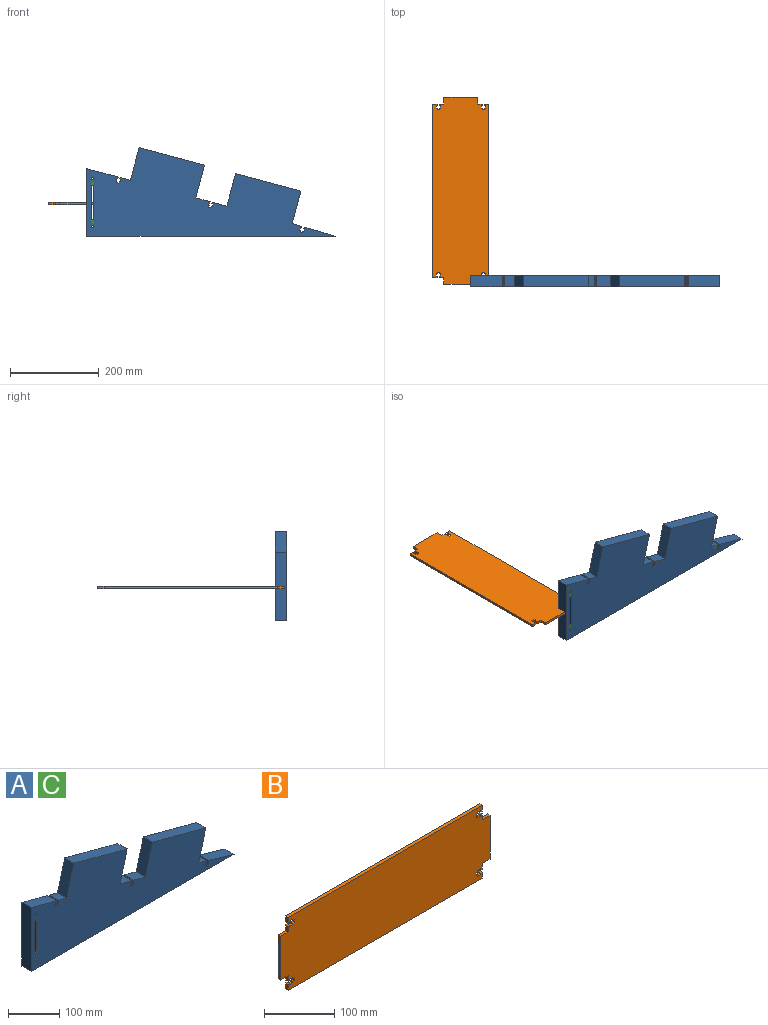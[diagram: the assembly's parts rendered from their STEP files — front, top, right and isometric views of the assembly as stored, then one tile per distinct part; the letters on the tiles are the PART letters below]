
ASSEMBLY  parts=3 mates=2
PART A: 55 faces, bbox 560.1x25.4x199.7 mm
  f0: plane 25.4x3.07mm, normal (-0.97,0,0.26), area 80.8mm2, adj f1,f52,f53,f54
  f1: plane 25.4x2.16mm, normal (-0.26,0,-0.97), area 56.8mm2, adj f0,f2,f53,f54
  f2: plane 25.4x6.11mm, normal (-0.97,0,0.26), area 160.6mm2, adj f1,f3,f53,f54
  f3: plane 25.4x2.16mm, normal (0.26,0,0.97), area 56.8mm2, adj f2,f4,f53,f54
  f4: plane 25.4x3.09mm, normal (-0.97,0,0.26), area 81.1mm2, adj f3,f5,f53,f54
  f5: plane 25.4x4.91mm, normal (0.26,0,0.97), area 129mm2, adj f4,f6,f53,f54
  f6: plane 25.4x3.11mm, normal (0.97,0,-0.26), area 81.7mm2, adj f5,f7,f53,f54
  f7: plane 25.4x2.16mm, normal (0.26,0,0.97), area 56.8mm2, adj f6,f8,f53,f54
  f8: plane 25.4x6.11mm, normal (0.97,0,-0.26), area 160.6mm2, adj f7,f9,f53,f54
  f9: plane 25.4x2.16mm, normal (-0.26,0,-0.97), area 56.8mm2, adj f8,f10,f53,f54
  f10: plane 25.4x3.05mm, normal (0.97,0,-0.26), area 80.3mm2, adj f9,f11,f53,f54
  f11: plane 70.28x25.4mm, normal (0.26,0,0.97), area 1848.2mm2, adj f10,f12,f53,f54
  f12: plane 152.4x25.4mm, normal (-1,0,0), area 3871mm2, adj f11,f13,f53,f54
  f13: plane 560.09x25.4mm, normal (0,0,-1), area 14226.3mm2, adj f12,f14,f53,f54
  f14: plane 70.86x25.4mm, normal (0.28,0,0.96), area 1874.8mm2, adj f13,f15,f53,f54
  f15: plane 25.4x3.06mm, normal (-0.96,0,0.28), area 81mm2, adj f14,f16,f53,f54
  f16: plane 25.4x2.15mm, normal (-0.28,0,-0.96), area 56.8mm2, adj f15,f17,f53,f54
  f17: plane 25.4x6.07mm, normal (-0.96,0,0.28), area 160.6mm2, adj f16,f18,f53,f54
  f18: plane 25.4x2.15mm, normal (0.28,0,0.96), area 56.8mm2, adj f17,f19,f53,f54
  f19: plane 25.4x3.06mm, normal (-0.96,0,0.28), area 81mm2, adj f18,f20,f53,f54
  f20: plane 25.4x4.73mm, normal (0.28,0,0.96), area 125.1mm2, adj f19,f21,f53,f54
  f21: plane 25.4x3.06mm, normal (0.96,0,-0.28), area 81mm2, adj f20,f22,f53,f54
  f22: plane 25.4x2.15mm, normal (0.28,0,0.96), area 56.8mm2, adj f21,f23,f53,f54
  f23: plane 25.4x6.07mm, normal (0.96,0,-0.28), area 160.6mm2, adj f22,f24,f53,f54
  f24: plane 25.4x2.15mm, normal (-0.28,0,-0.96), area 56.8mm2, adj f23,f25,f53,f54
  f25: plane 25.4x3.06mm, normal (0.96,0,-0.28), area 81mm2, adj f24,f26,f53,f54
  f26: plane 25.4x21.97mm, normal (0.28,0,0.96), area 581.3mm2, adj f25,f27,f53,f54
  f27: plane 73.6x25.4mm, normal (0.97,0,-0.26), area 1935.5mm2, adj f26,f28,f53,f54
  f28: plane 147.21x39.44mm, normal (0.26,0,0.97), area 3871mm2, adj f27,f29,f53,f54
  f29: plane 73.6x25.4mm, normal (-0.97,0,0.26), area 1935.5mm2, adj f28,f30,f53,f54
  f30: plane 32.66x25.4mm, normal (0.26,0,0.97), area 859mm2, adj f29,f31,f53,f54
  f31: plane 25.4x3.08mm, normal (-0.97,0,0.26), area 81mm2, adj f30,f32,f53,f54
  f32: plane 25.4x2.16mm, normal (-0.26,0,-0.97), area 56.8mm2, adj f31,f33,f53,f54
  f33: plane 25.4x6.11mm, normal (-0.97,0,0.26), area 160.6mm2, adj f32,f34,f53,f54
  f34: plane 25.4x2.16mm, normal (0.26,0,0.97), area 56.8mm2, adj f33,f35,f53,f54
  f35: plane 25.4x3.08mm, normal (-0.97,0,0.26), area 81mm2, adj f34,f36,f53,f54
  f36: plane 25.4x4.66mm, normal (0.26,0,0.97), area 122.6mm2, adj f35,f37,f53,f54
  f37: plane 25.4x3.08mm, normal (0.97,0,-0.26), area 81mm2, adj f36,f38,f53,f54
  f38: plane 25.4x2.16mm, normal (0.26,0,0.97), area 56.8mm2, adj f37,f39,f53,f54
  f39: plane 25.4x6.11mm, normal (0.97,0,-0.26), area 160.6mm2, adj f38,f40,f53,f54
  f40: plane 25.4x2.16mm, normal (-0.26,0,-0.97), area 56.8mm2, adj f39,f41,f53,f54
  f41: plane 25.4x3.08mm, normal (0.97,0,-0.26), area 81mm2, adj f40,f42,f53,f54
  f42: plane 32.66x25.4mm, normal (0.26,0,0.97), area 858.7mm2, adj f41,f43,f53,f54
  f43: plane 73.6x25.4mm, normal (0.97,0,-0.26), area 1935.5mm2, adj f42,f44,f53,f54
  f44: plane 147.21x39.44mm, normal (0.26,0,0.97), area 3871mm2, adj f43,f45,f53,f54
  f45: plane 73.6x25.4mm, normal (-0.97,0,0.26), area 1935.5mm2, adj f44,f52,f53,f54
  f46: plane 76.2x25.4mm, normal (-1,0,0), area 1935.5mm2, adj f47,f51,f53,f54
  f47: plane 25.4x5.08mm, normal (0,0,1), area 129mm2, adj f46,f48,f53,f54
  f48: plane 76.2x25.4mm, normal (1,0,0), area 1935.5mm2, adj f47,f51,f53,f54
  f49: cylinder r=2.54mm len=25.4mm, axis (0,1,0), area 405.4mm2, adj f53,f54
  f50: cylinder r=2.54mm len=25.4mm, axis (0,1,0), area 405.4mm2, adj f53,f54
  f51: plane 25.4x5.08mm, normal (0,0,-1), area 129mm2, adj f46,f48,f53,f54
  f52: plane 25.4x22.95mm, normal (0.26,0,0.97), area 603.4mm2, adj f0,f45,f53,f54
  f53: plane 560.09x199.71mm, normal (0,-1,0), area 65741.3mm2, adj f0,f1,f2,f3,f4,f5,f6,f7
  f54: plane 560.09x199.71mm, normal (0,1,0), area 65741.3mm2, adj f0,f1,f2,f3,f4,f5,f6,f7
PART B: 62 faces, bbox 421.6x5.1x127 mm
  f0: plane 76.2x5.08mm, normal (-1,0,0), area 387.1mm2, adj f1,f59,f60,f61
  f1: plane 15.24x5.08mm, normal (0,0,-1), area 77.4mm2, adj f0,f2,f60,f61
  f2: plane 10.16x5.08mm, normal (-1,0,0), area 51.6mm2, adj f1,f3,f60,f61
  f3: plane 5.08x3.19mm, normal (0,0,-1), area 16.2mm2, adj f2,f4,f60,f61
  f4: plane 5.08x2.24mm, normal (1,0,0), area 11.4mm2, adj f3,f5,f60,f61
  f5: plane 6.32x5.08mm, normal (0,0,-1), area 32.1mm2, adj f4,f6,f60,f61
  f6: plane 5.08x2.24mm, normal (-1,0,0), area 11.4mm2, adj f5,f7,f60,f61
  f7: plane 5.08x3.19mm, normal (0,0,-1), area 16.2mm2, adj f6,f8,f60,f61
  f8: plane 5.08x5.08mm, normal (-1,0,0), area 25.8mm2, adj f7,f9,f60,f61
  f9: plane 5.08x3.19mm, normal (0,0,1), area 16.2mm2, adj f8,f10,f60,f61
  f10: plane 5.08x2.24mm, normal (-1,0,0), area 11.4mm2, adj f9,f11,f60,f61
  f11: plane 6.32x5.08mm, normal (0,0,1), area 32.1mm2, adj f10,f12,f60,f61
  f12: plane 5.08x2.24mm, normal (1,0,0), area 11.4mm2, adj f11,f13,f60,f61
  f13: plane 5.08x3.19mm, normal (0,0,1), area 16.2mm2, adj f12,f14,f60,f61
  f14: plane 10.16x5.08mm, normal (-1,0,0), area 51.6mm2, adj f13,f15,f60,f61
  f15: plane 391.16x5.08mm, normal (0,0,-1), area 1987.1mm2, adj f14,f16,f60,f61
  f16: plane 10.16x5.08mm, normal (1,0,0), area 51.6mm2, adj f15,f17,f60,f61
  f17: plane 5.08x3.18mm, normal (0,0,1), area 16.2mm2, adj f16,f18,f60,f61
  f18: plane 5.08x2.24mm, normal (-1,0,0), area 11.4mm2, adj f17,f19,f60,f61
  f19: plane 6.32x5.08mm, normal (0,0,1), area 32.1mm2, adj f18,f20,f60,f61
  f20: plane 5.08x2.24mm, normal (1,0,0), area 11.4mm2, adj f19,f21,f60,f61
  f21: plane 5.08x3.19mm, normal (0,0,1), area 16.2mm2, adj f20,f22,f60,f61
  f22: plane 5.08x5.08mm, normal (1,0,0), area 25.8mm2, adj f21,f23,f60,f61
  f23: plane 5.08x3.22mm, normal (0,0,-1), area 16.3mm2, adj f22,f24,f60,f61
  f24: plane 5.08x2.24mm, normal (1,0,0), area 11.4mm2, adj f23,f25,f60,f61
  f25: plane 6.32x5.08mm, normal (0,0,-1), area 32.1mm2, adj f24,f26,f60,f61
  f26: plane 5.08x2.24mm, normal (-1,0,0), area 11.4mm2, adj f25,f27,f60,f61
  f27: plane 5.08x3.16mm, normal (0,0,-1), area 16.1mm2, adj f26,f28,f60,f61
  f28: plane 10.16x5.08mm, normal (1,0,0), area 51.6mm2, adj f27,f29,f60,f61
  f29: plane 15.24x5.08mm, normal (0,0,-1), area 77.4mm2, adj f28,f30,f60,f61
  f30: plane 76.2x5.08mm, normal (1,0,0), area 387.1mm2, adj f29,f31,f60,f61
  f31: plane 15.24x5.08mm, normal (0,0,1), area 77.4mm2, adj f30,f32,f60,f61
  f32: plane 10.16x5.08mm, normal (1,0,0), area 51.6mm2, adj f31,f33,f60,f61
  f33: plane 5.08x3.18mm, normal (0,0,1), area 16.2mm2, adj f32,f34,f60,f61
  f34: plane 5.08x2.24mm, normal (-1,0,0), area 11.4mm2, adj f33,f35,f60,f61
  f35: plane 6.32x5.08mm, normal (0,0,1), area 32.1mm2, adj f34,f36,f60,f61
  f36: plane 5.08x2.24mm, normal (1,0,0), area 11.4mm2, adj f35,f37,f60,f61
  f37: plane 5.08x3.19mm, normal (0,0,1), area 16.2mm2, adj f36,f38,f60,f61
  f38: plane 5.08x5.08mm, normal (1,0,0), area 25.8mm2, adj f37,f39,f60,f61
  f39: plane 5.08x3.22mm, normal (0,0,-1), area 16.3mm2, adj f38,f40,f60,f61
  f40: plane 5.08x2.24mm, normal (1,0,0), area 11.4mm2, adj f39,f41,f60,f61
  f41: plane 6.32x5.08mm, normal (0,0,-1), area 32.1mm2, adj f40,f42,f60,f61
  f42: plane 5.08x2.24mm, normal (-1,0,0), area 11.4mm2, adj f41,f43,f60,f61
  f43: plane 5.08x3.16mm, normal (0,0,-1), area 16.1mm2, adj f42,f44,f60,f61
  f44: plane 10.16x5.08mm, normal (1,0,0), area 51.6mm2, adj f43,f45,f60,f61
  f45: plane 391.16x5.08mm, normal (0,0,1), area 1987.1mm2, adj f44,f46,f60,f61
  f46: plane 10.16x5.08mm, normal (-1,0,0), area 51.6mm2, adj f45,f47,f60,f61
  f47: plane 5.08x3.19mm, normal (0,0,-1), area 16.2mm2, adj f46,f48,f60,f61
  f48: plane 5.08x2.24mm, normal (1,0,0), area 11.4mm2, adj f47,f49,f60,f61
  f49: plane 6.32x5.08mm, normal (0,0,-1), area 32.1mm2, adj f48,f50,f60,f61
  f50: plane 5.08x2.24mm, normal (-1,0,0), area 11.4mm2, adj f49,f51,f60,f61
  f51: plane 5.08x3.19mm, normal (0,0,-1), area 16.2mm2, adj f50,f52,f60,f61
  f52: plane 5.08x5.08mm, normal (-1,0,0), area 25.8mm2, adj f51,f53,f60,f61
  f53: plane 5.08x3.19mm, normal (0,0,1), area 16.2mm2, adj f52,f54,f60,f61
  f54: plane 5.08x2.24mm, normal (-1,0,0), area 11.4mm2, adj f53,f55,f60,f61
  f55: plane 6.32x5.08mm, normal (0,0,1), area 32.1mm2, adj f54,f56,f60,f61
  f56: plane 5.08x2.24mm, normal (1,0,0), area 11.4mm2, adj f55,f57,f60,f61
  f57: plane 5.08x3.19mm, normal (0,0,1), area 16.2mm2, adj f56,f58,f60,f61
  f58: plane 10.16x5.08mm, normal (-1,0,0), area 51.6mm2, adj f57,f59,f60,f61
  f59: plane 15.24x5.08mm, normal (0,0,1), area 77.4mm2, adj f0,f58,f60,f61
  f60: plane 421.64x127mm, normal (0,-1,0), area 51628.7mm2, adj f0,f1,f2,f3,f4,f5,f6,f7
  f61: plane 421.64x127mm, normal (0,1,0), area 51628.7mm2, adj f0,f1,f2,f3,f4,f5,f6,f7
PART C: same geometry as A
PLACE A t=(150.7,-95.47,88.37)mm
PLACE B rot(axis=(-0.58,0.58,-0.58),120deg) t=(-544.21,95.03,17.98)mm
PLACE C t=(150.7,-95.47,88.37)mm
MATE slider B.f31 <-> C.f46  axis (1,0,0) through (-506.11,-108.17,23.06)mm
MATE parallel B.f30 <-> C.f53  axis (0,-1,0) through (-544.21,-115.79,20.52)mm
